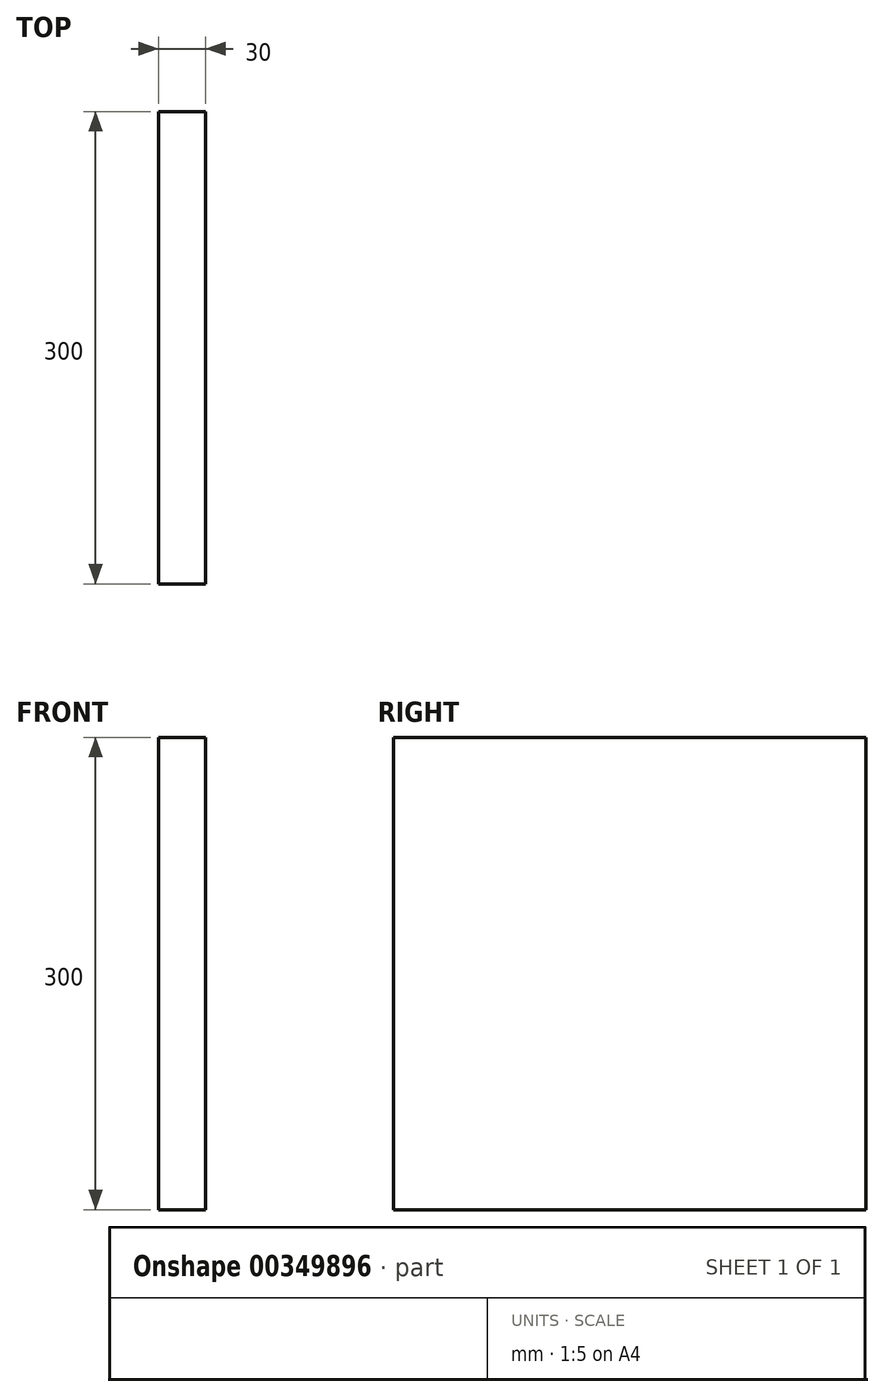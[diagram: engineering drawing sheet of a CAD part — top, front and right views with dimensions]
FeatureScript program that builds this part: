
annotation { "Feature Type Name" : "Feature", "Feature Type Description" : "" }
export const myFeature = defineFeature(function(context is Context, id is Id, definition is map)
    precondition{}
    {
        {
            var Q0;
            Q0=qCreatedBy(makeId("Right.planeOp"),FACE);
            var sketch = newSketch(context, id + "F0", { "sketchPlane" : qUnion([Q0])});
            skLineSegment(sketch, "E0.bottom", {"start": v(150, -150) * mm, "end": v(-150, -150) * mm});
            skLineSegment(sketch, "E0.top", {"start": v(150, 150) * mm, "end": v(-150, 150) * mm});
            skLineSegment(sketch, "E0.left", {"start": v(150, -150) * mm, "end": v(150, 150) * mm});
            skLineSegment(sketch, "E0.right", {"start": v(-150, -150) * mm, "end": v(-150, 150) * mm});
            skPoint(sketch, "E0.middle", {"position": v(0, 0) * mm});
            skSolve(sketch);
        }
        {
            var Q0;
            Q0=makeQuery(id+"F0.imprint","IMPRINT",FACE,{"disambiguationData":[TD([[makeQuery(id+"F0.imprint","IMPRINT",EDGE,{"derivedFrom":sQuery(id+"F0.wireOp",EDGE,"E0.bottom")}),-1.0]])]});
            extrude(context, id + "F1", {"entities" : qUnion([Q0]), "depth" : 30 * mm});
        }
    });
